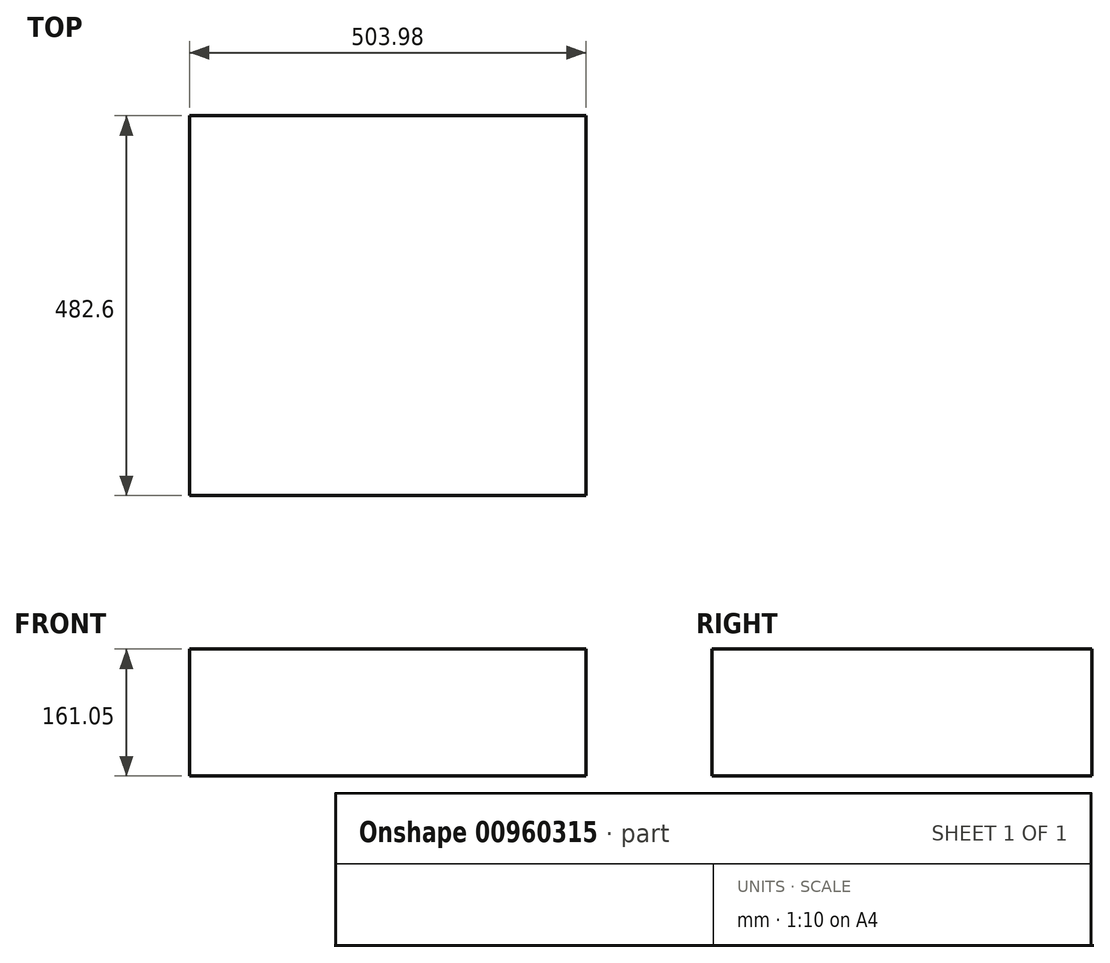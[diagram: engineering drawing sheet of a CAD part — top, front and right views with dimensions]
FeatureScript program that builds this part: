
annotation { "Feature Type Name" : "Feature", "Feature Type Description" : "" }
export const myFeature = defineFeature(function(context is Context, id is Id, definition is map)
    precondition{}
    {
        {
            var Q0;
            Q0=qCreatedBy(makeId("Front.planeOp"),FACE);
            var sketch = newSketch(context, id + "F0", { "sketchPlane" : qUnion([Q0])});
            skLineSegment(sketch, "E0.bottom", {"start": v(15.98, 31.41) * mm, "end": v(519.96, 31.41) * mm});
            skLineSegment(sketch, "E0.top", {"start": v(15.98, -129.64) * mm, "end": v(519.96, -129.64) * mm});
            skLineSegment(sketch, "E0.left", {"start": v(15.98, 31.41) * mm, "end": v(15.98, -129.64) * mm});
            skLineSegment(sketch, "E0.right", {"start": v(519.96, 31.41) * mm, "end": v(519.96, -129.64) * mm});
            skSolve(sketch);
        }
        {
            var Q0;
            Q0=makeQuery(id+"F0.imprint","IMPRINT",FACE,{"disambiguationData":[TD([[makeQuery(id+"F0.imprint","IMPRINT",EDGE,{"derivedFrom":sQuery(id+"F0.wireOp",EDGE,"E0.bottom")}),-1.0]])]});
            var Q1;
            Q1=sQuery(id+"F0.wireOp",EDGE,"E0.top");
            var Q2;
            Q2=sQuery(id+"F0.wireOp",EDGE,"E0.left");
            var Q3;
            Q3=sQuery(id+"F0.wireOp",EDGE,"E0.bottom");
            var Q4;
            Q4=sQuery(id+"F0.wireOp",EDGE,"E0.right");
            extrude(context, id + "F1", {"entities" : qUnion([Q0]), "bodyType" : ToolBodyType.SURFACE, "operationType" : NewBodyOperationType.ADD, "surfaceEntities" : qUnion([Q1, Q2, Q3, Q4]), "depth" : 482.6 * mm, "offsetDistance" : 25.4 * mm});
        }
    });
